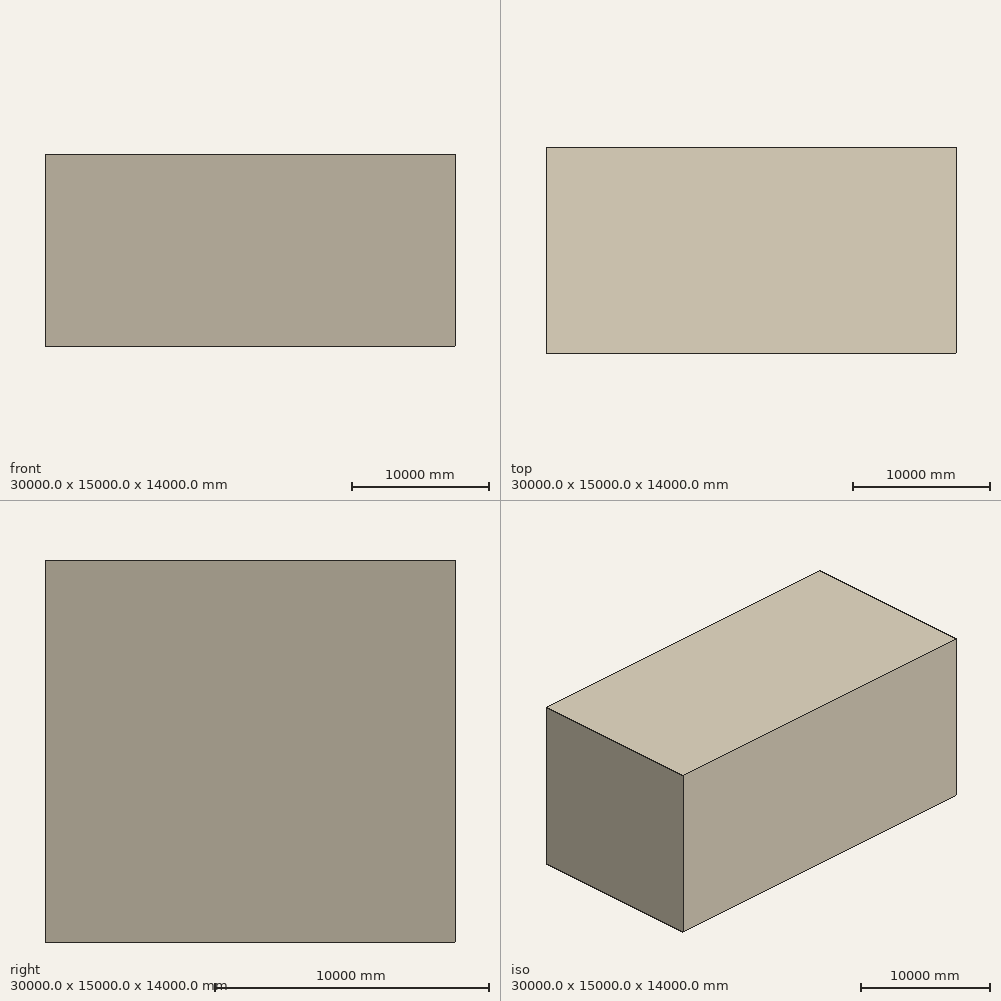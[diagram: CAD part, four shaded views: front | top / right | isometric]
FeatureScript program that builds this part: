
annotation { "Feature Type Name" : "Feature", "Feature Type Description" : "" }
export const myFeature = defineFeature(function(context is Context, id is Id, definition is map)
    precondition{}
    {
        {
            var Q0;
            Q0=qCreatedBy(makeId("Top.planeOp"),FACE);
            var sketch = newSketch(context, id + "F0", { "sketchPlane" : qUnion([Q0])});
            skLineSegment(sketch, "E0.bottom", {"start": v(-15000, 7500) * mm, "end": v(15000, 7500) * mm});
            skLineSegment(sketch, "E0.top", {"start": v(-15000, -7500) * mm, "end": v(15000, -7500) * mm});
            skLineSegment(sketch, "E0.left", {"start": v(-15000, 7500) * mm, "end": v(-15000, -7500) * mm});
            skLineSegment(sketch, "E0.right", {"start": v(15000, 7500) * mm, "end": v(15000, -7500) * mm});
            skSolve(sketch);
        }
        {
            var Q0;
            Q0=makeQuery(id+"F0.imprint","IMPRINT",FACE,{"disambiguationData":[TD([[makeQuery(id+"F0.imprint","IMPRINT",EDGE,{"derivedFrom":sQuery(id+"F0.wireOp",EDGE,"E0.bottom")}),-1.0]])]});
            extrude(context, id + "F1", {"entities" : qUnion([Q0]), "depth" : 7000 * mm, "offsetDistance" : 25 * mm, "hasSecondDirection" : true, "secondDirectionOppositeDirection" : true, "secondDirectionDepth" : 7000 * mm});
        }
    });
